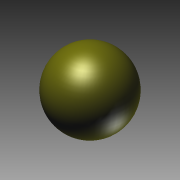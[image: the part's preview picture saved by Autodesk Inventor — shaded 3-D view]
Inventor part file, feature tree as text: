
AUTODESK INVENTOR PART (.ipt)
format: ipt  version: 2011 SP1 (Build 150282100, 282)  size: 109,056 bytes
history: native  units: mm
features: revolve x1, sketch x1
ambient origin geometry x8: Origin, YZ Plane, XZ Plane, XY Plane, X Axis, Y Axis, Z Axis, Center Point
bodies: Solid1 (feature_tree)
feature tree (2):
  revolve  "Revolution1"  [1 undecoded]
  sketch  "Sketch_4"  dims[d0=360.0deg]
note: 1 required parameter value undecoded (feature->parameter linkage not recoverable at this tier; creation-order binding heuristic only, values carry confidence <= 0.55)
